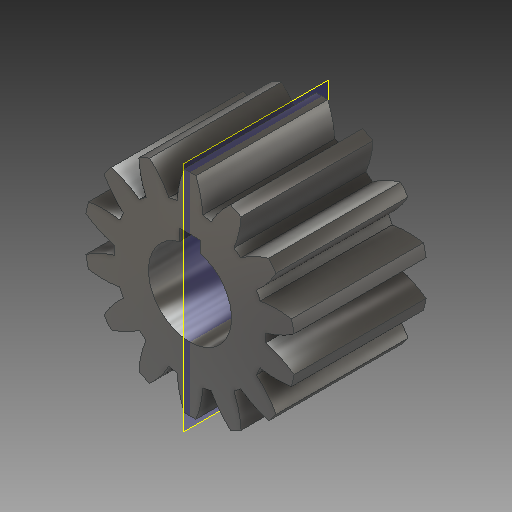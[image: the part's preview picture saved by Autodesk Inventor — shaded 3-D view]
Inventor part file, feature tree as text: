
AUTODESK INVENTOR PART (.ipt)
format: ipt  version: 2018 (Build 220112000, 112)  size: 248,320 bytes
history: native  units: in
note: dims shown in document units (in); Inventor stores cm internally (conversion verified against a paired STEP export)
features: plane x1, imported_body x1
ambient origin geometry x8: Origin, YZ Plane, XZ Plane, XY Plane, X Axis, Y Axis, Z Axis, Center Point
bodies: Solid1 (feature_tree)
feature tree (2):
  plane  "Work Plane3"
  imported_body  "Imported1"
